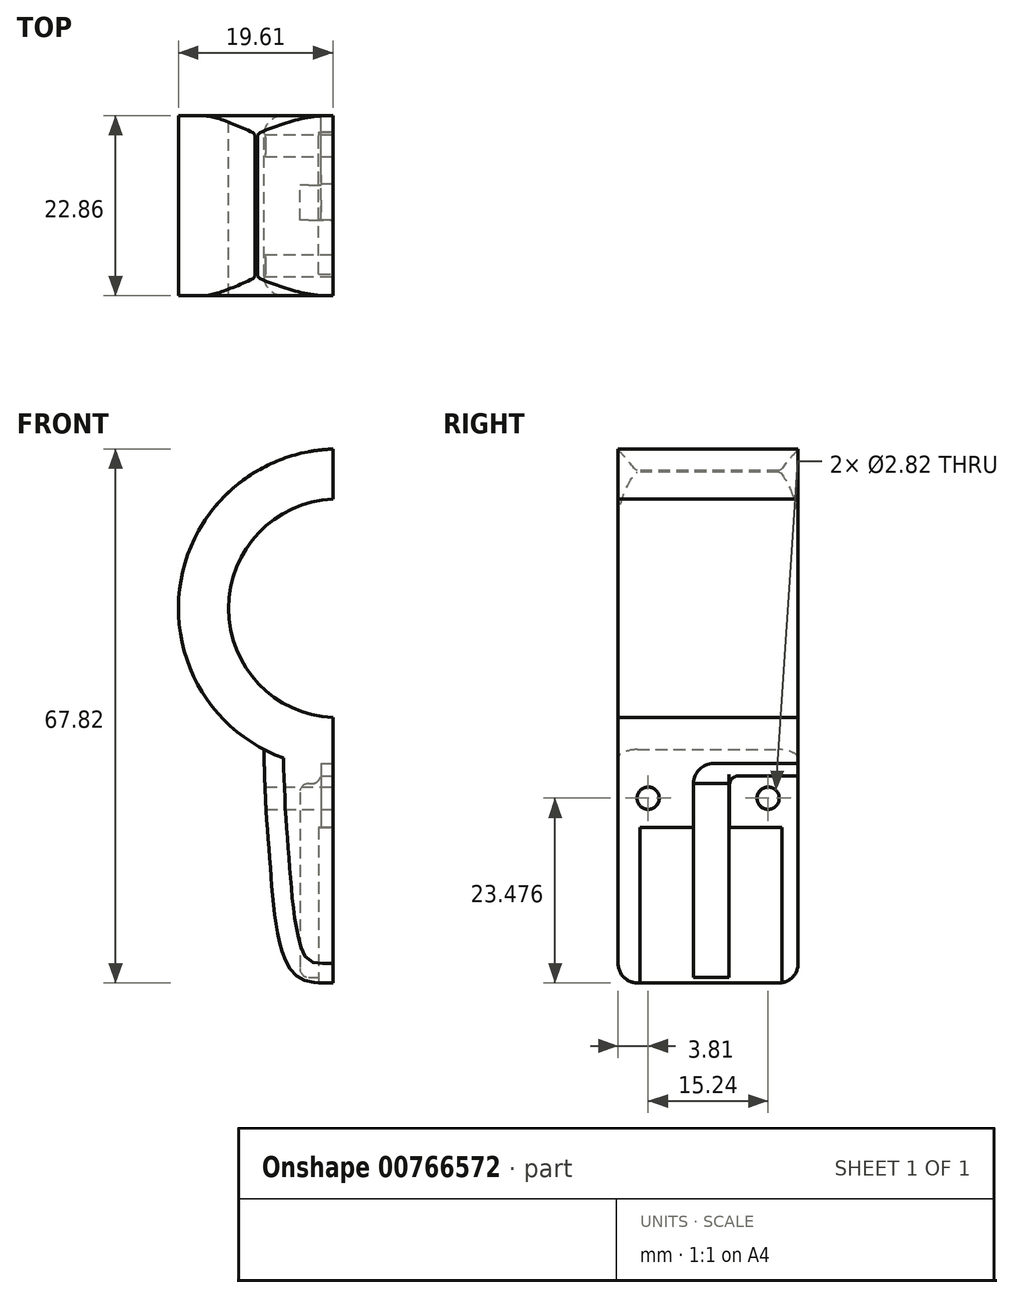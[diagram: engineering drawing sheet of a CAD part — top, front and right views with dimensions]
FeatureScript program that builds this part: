
annotation { "Feature Type Name" : "Feature", "Feature Type Description" : "" }
export const myFeature = defineFeature(function(context is Context, id is Id, definition is map)
    precondition{}
    {
        {
            var Q0;
            Q0=qCreatedBy(makeId("Front.planeOp"),FACE);
            var sketch = newSketch(context, id + "F0", { "sketchPlane" : qUnion([Q0])});
            skCircle(sketch, "E0", {"center": v(0, 0) * mm, "radius": 13.9 * mm});
            skCircle(sketch, "E1.0", {"center": v(0, 0) * mm, "radius": 20.24 * mm});
            skFitSpline(sketch, "E2", {"points": [v(-10.48, 17.32) * mm, v(-6.62, 22.45) * mm, v(-5.79, 30.49) * mm, v(0, 31.88) * mm, v(5.12, 30.56) * mm, v(6.08, 23.46) * mm, v(9.7, 17.76) * mm], "startDerivative": vector(26.15, 14.41) * mm, "endDerivative": vector(40.23, -23.63) * mm});
            skFitSpline(sketch, "E3", {"points": [v(-9.4, -17.93) * mm, v(-8.61, -32.2) * mm, v(-5.82, -46.1) * mm, v(0, -47.57) * mm, v(6.45, -45.96) * mm, v(9.7, -28.64) * mm, v(9.7, -17.76) * mm], "startDerivative": vector(4.47, -161.39) * mm, "endDerivative": vector(-1.33, 64.22) * mm});
            skSolve(sketch);
        }
        {
            var Q0;
            Q0=makeQuery(id+"F0.imprint","IMPRINT",FACE,{"disambiguationData":[TD([[makeQuery(id+"F0.imprint","IMPRINT",EDGE,{"derivedFrom":sQuery(id+"F0.wireOp",EDGE,"E0")}),-1.0]])]});
            var Q1;
            {var subQ0=sQuery(id+"F0.wireOp",EDGE,"E3");Q1=makeQuery(id+"F0.imprint","IMPRINT",FACE,{"disambiguationData":[TD([[makeQuery(id+"F0.imprint","IMPRINT",EDGE,{"derivedFrom":subQ0}),1.0]])]});}
            var Q2;
            {var subQ0=sQuery(id+"F0.wireOp",EDGE,"E2");var subQ1=sQuery(id+"F0.wireOp",EDGE,"E1.0");var subQ2=makeQuery(id+"F0.imprint","INTERSECT",VERTEX,{"disambiguationData":[OD(1.0)],"derivedFrom":[subQ1,subQ0]});Q2=makeQuery(id+"F0.imprint","IMPRINT",FACE,{"disambiguationData":[TD([[makeQuery(id+"F0.imprint","IMPRINT",EDGE,{"disambiguationData":[TD([[subQ2,-1.0]])],"derivedFrom":subQ1}),-1.0]])]});}
            extrude(context, id + "F1", {"entities" : qUnion([Q0, Q1, Q2]), "depth" : 22.86 * mm, "offsetDistance" : 25.4 * mm});
        }
        {
            var Q0;
            Q0=qCreatedBy(makeId("Right.planeOp"),FACE);
            var sketch = newSketch(context, id + "F2", { "sketchPlane" : qUnion([Q0])});
            skCircle(sketch, "E4", {"center": v(-10.97, 26.33) * mm, "radius": 1.9 * mm});
            skCircle(sketch, "E5", {"center": v(-19.05, -24.11) * mm, "radius": 1.41 * mm});
            skCircle(sketch, "E6", {"center": v(-3.81, -24.11) * mm, "radius": 1.41 * mm});
            skSolve(sketch);
        }
        {
            var Q0;
            Q0=qSketchRegion(id+"F2",true);
            extrude(context, id + "F3", {"entities" : qUnion([Q0]), "operationType" : NewBodyOperationType.REMOVE, "endBound" : BoundingType.SYMMETRIC, "oppositeDirection" : true, "depth" : 25.4 * mm, "offsetDistance" : 25.4 * mm});
        }
        {
            var Q0;
            Q0=qCreatedBy(makeId("Front.planeOp"),FACE);
            var sketch = newSketch(context, id + "F4", { "sketchPlane" : qUnion([Q0])});
            skLineSegment(sketch, "E7.bottom", {"start": v(-0.64, 36.94) * mm, "end": v(30.33, 36.94) * mm});
            skLineSegment(sketch, "E7.top", {"start": v(-0.64, -50.47) * mm, "end": v(30.33, -50.47) * mm});
            skLineSegment(sketch, "E7.left", {"start": v(-0.64, 36.94) * mm, "end": v(-0.64, -50.47) * mm});
            skLineSegment(sketch, "E7.right", {"start": v(30.33, 36.94) * mm, "end": v(30.33, -50.47) * mm});
            skSolve(sketch);
        }
        {
            var Q0;
            Q0=makeQuery(id+"F4.imprint","IMPRINT",FACE,{"disambiguationData":[TD([[makeQuery(id+"F4.imprint","IMPRINT",EDGE,{"derivedFrom":sQuery(id+"F4.wireOp",EDGE,"E7.bottom")}),-1.0]])]});
            extrude(context, id + "F5", {"entities" : qUnion([Q0]), "operationType" : NewBodyOperationType.REMOVE, "depth" : 25.4 * mm, "offsetDistance" : 25.4 * mm});
        }
        {
            var Q0;
            Q0=makeQuery(id+"F1.opExtrude","CAP_EDGE",EDGE,{"disambiguationData":[OSD([sQuery(id+"F0.wireOp",EDGE,"E2")])],"isStart":false});
            var Q1;
            {var subQ0=sQuery(id+"F0.wireOp",EDGE,"E1.0");Q1=makeQuery(id+"F1.opExtrude","CAP_EDGE",EDGE,{"disambiguationData":[OSD([subQ0]),TDD([makeQuery(id+"F0.imprint","IMPRINT",EDGE,{"disambiguationData":[TD([[makeQuery(id+"F0.imprint","INTERSECT",VERTEX,{"disambiguationData":[OD(0.0)],"derivedFrom":[subQ0,sQuery(id+"F0.wireOp",EDGE,"E2")]}),-1.0]])],"derivedFrom":subQ0})])],"isStart":false});}
            var Q2;
            Q2=makeQuery(id+"F1.opExtrude","CAP_EDGE",EDGE,{"disambiguationData":[OSD([sQuery(id+"F0.wireOp",EDGE,"E3")])],"isStart":false});
            var Q3;
            Q3=makeQuery(id+"F1.opExtrude","CAP_EDGE",EDGE,{"disambiguationData":[OSD([sQuery(id+"F0.wireOp",EDGE,"E2")])],"isStart":true});
            var Q4;
            {var subQ0=sQuery(id+"F0.wireOp",EDGE,"E1.0");Q4=makeQuery(id+"F1.opExtrude","CAP_EDGE",EDGE,{"disambiguationData":[OSD([subQ0]),TDD([makeQuery(id+"F0.imprint","IMPRINT",EDGE,{"disambiguationData":[TD([[makeQuery(id+"F0.imprint","INTERSECT",VERTEX,{"disambiguationData":[OD(0.0)],"derivedFrom":[subQ0,sQuery(id+"F0.wireOp",EDGE,"E2")]}),-1.0]])],"derivedFrom":subQ0})])],"isStart":true});}
            var Q5;
            Q5=makeQuery(id+"F1.opExtrude","CAP_EDGE",EDGE,{"disambiguationData":[OSD([sQuery(id+"F0.wireOp",EDGE,"E3")])],"isStart":true});
            fillet(context, id + "F6", {"entities" : qUnion([Q0, Q1, Q2, Q3, Q4, Q5]), "radius" : 2.45 * mm, "tangentPropagation" : true, "allowEdgeOverflow" : false});
        }
        {
            var Q0;
            {var subQ1=sQuery(id+"F0.wireOp",EDGE,"E3");Q0=makeQuery(id+"F5.boolean.opBoolean","COPY",FACE,{"disambiguationData":[TD([makeQuery(id+"F1.opExtrude","SWEPT_FACE",FACE,{"disambiguationData":[OSD([subQ1])]})])],"derivedFrom":makeQuery(id+"F5.opExtrude","SWEPT_FACE",FACE,{"disambiguationData":[OSD([sQuery(id+"F4.wireOp",EDGE,"E7.left")])]})});}
            var sketch = newSketch(context, id + "F7", { "sketchPlane" : qUnion([Q0])});
            skLineSegment(sketch, "E8.bottom", {"start": v(-20.1, -27.85) * mm, "end": v(-2.07, -27.85) * mm});
            skLineSegment(sketch, "E8.top", {"start": v(-20.1, -51.03) * mm, "end": v(-2.07, -51.03) * mm});
            skLineSegment(sketch, "E8.left", {"start": v(-20.1, -27.85) * mm, "end": v(-20.1, -51.03) * mm});
            skLineSegment(sketch, "E8.right", {"start": v(-2.07, -27.85) * mm, "end": v(-2.07, -51.03) * mm});
            skSolve(sketch);
        }
        {
            var Q0;
            {var subQ0=sQuery(id+"F7.wireOp",EDGE,"E8.bottom");Q0=makeQuery(id+"F7.imprint","IMPRINT",FACE,{"disambiguationData":[TD([[makeQuery(id+"F7.imprint","IMPRINT",EDGE,{"derivedFrom":subQ0}),-1.0]])]});}
            var Q1;
            {var subQ0=sQuery(id+"F7.wireOp",EDGE,"E8.top");Q1=makeQuery(id+"F7.imprint","IMPRINT",FACE,{"disambiguationData":[TD([[makeQuery(id+"F7.imprint","IMPRINT",EDGE,{"derivedFrom":subQ0}),1.0]])]});}
            extrude(context, id + "F8", {"entities" : qUnion([Q0, Q1]), "operationType" : NewBodyOperationType.REMOVE, "oppositeDirection" : true, "depth" : 1.78 * mm, "offsetDistance" : 25.4 * mm});
        }
        {
            var Q0;
            {var subQ1=sQuery(id+"F0.wireOp",EDGE,"E3");Q0=makeQuery(id+"F5.boolean.opBoolean","COPY",FACE,{"disambiguationData":[TD([makeQuery(id+"F1.opExtrude","SWEPT_FACE",FACE,{"disambiguationData":[OSD([subQ1])]})])],"derivedFrom":makeQuery(id+"F5.opExtrude","SWEPT_FACE",FACE,{"disambiguationData":[OSD([sQuery(id+"F4.wireOp",EDGE,"E7.left")])]})});}
            var sketch = newSketch(context, id + "F9", { "sketchPlane" : qUnion([Q0])});
            skLineSegment(sketch, "E9.bottom", {"start": v(-10.74, -19.72) * mm, "end": v(-8.7, -19.72) * mm});
            skLineSegment(sketch, "E9.top", {"start": v(-13.28, -31.32) * mm, "end": v(-8.7, -31.32) * mm});
            skLineSegment(sketch, "E9.left", {"start": v(-13.28, -22.26) * mm, "end": v(-13.28, -31.32) * mm});
            skLineSegment(sketch, "E9.right", {"start": v(-8.7, -21.27) * mm, "end": v(-8.7, -31.32) * mm});
            skLineSegment(sketch, "E10.bottom", {"start": v(-8.7, -19.72) * mm, "end": v(0.09, -19.72) * mm});
            skLineSegment(sketch, "E10.top", {"start": v(-8.7, -21.27) * mm, "end": v(0.09, -21.27) * mm});
            skLineSegment(sketch, "E10.right", {"start": v(0.09, -19.72) * mm, "end": v(0.09, -21.27) * mm});
            skPoint(sketch, "E11.visualSharp", {"position": v(-13.28, -19.72) * mm});
            skArc(sketch, "E11.filletArc", {"start": v(-10.74, -19.72) * mm, "mid": v(-12.54, -20.47) * mm, "end": v(-13.28, -22.26) * mm});
            skSolve(sketch);
        }
        {
            var Q0;
            {var subQ1=sQuery(id+"F9.wireOp",EDGE,"E9.bottom");Q0=makeQuery(id+"F9.imprint","IMPRINT",FACE,{"disambiguationData":[TD([[makeQuery(id+"F9.imprint","IMPRINT",EDGE,{"derivedFrom":subQ1}),-1.0]])]});}
            var Q1;
            {var subQ0=sQuery(id+"F9.wireOp",EDGE,"E9.top");Q1=makeQuery(id+"F9.imprint","IMPRINT",FACE,{"disambiguationData":[TD([[makeQuery(id+"F9.imprint","IMPRINT",EDGE,{"derivedFrom":subQ0}),1.0]])]});}
            extrude(context, id + "F10", {"entities" : qUnion([Q0, Q1]), "operationType" : NewBodyOperationType.REMOVE, "oppositeDirection" : true, "depth" : 1.52 * mm, "offsetDistance" : 25.4 * mm});
        }
        {
            var Q0;
            {var subQ0=sQuery(id+"F0.wireOp",EDGE,"E3");var subQ3=sQuery(id+"F0.wireOp",EDGE,"E0");var subQ5=makeQuery(id+"F1.opExtrude","SWEPT_FACE",FACE,{"disambiguationData":[OSD([subQ3])]});var subQ7=makeQuery(id+"F1.opExtrude","SWEPT_FACE",FACE,{"disambiguationData":[OSD([subQ0])]});Q0=makeQuery(id+"F10.boolean.opBoolean","SPLIT",FACE,{"disambiguationData":[TD([subQ5])],"derivedFrom":makeQuery(id+"F5.boolean.opBoolean","COPY",FACE,{"disambiguationData":[TD([subQ7])],"derivedFrom":makeQuery(id+"F5.opExtrude","SWEPT_FACE",FACE,{"disambiguationData":[OSD([sQuery(id+"F4.wireOp",EDGE,"E7.left")])]})})});}
            var sketch = newSketch(context, id + "F11", { "sketchPlane" : qUnion([Q0])});
            skLineSegment(sketch, "E12.bottom", {"start": v(-13.28, -22.26) * mm, "end": v(-8.8, -22.26) * mm});
            skLineSegment(sketch, "E12.top", {"start": v(-13.28, -46.86) * mm, "end": v(-8.8, -46.86) * mm});
            skLineSegment(sketch, "E12.left", {"start": v(-13.28, -22.26) * mm, "end": v(-13.28, -46.86) * mm});
            skLineSegment(sketch, "E12.right", {"start": v(-8.8, -22.26) * mm, "end": v(-8.8, -46.86) * mm});
            skSolve(sketch);
        }
        {
            var Q0;
            {var subQ1=sQuery(id+"F11.wireOp",EDGE,"E12.bottom");Q0=makeQuery(id+"F11.imprint","IMPRINT",FACE,{"disambiguationData":[TD([[makeQuery(id+"F11.imprint","IMPRINT",EDGE,{"derivedFrom":subQ1}),-1.0]])]});}
            extrude(context, id + "F12", {"entities" : qUnion([Q0]), "operationType" : NewBodyOperationType.REMOVE, "oppositeDirection" : true, "depth" : 4.2 * mm, "offsetDistance" : 25.4 * mm});
        }
        {
            var Q0;
            Q0=makeQuery(id+"F12.boolean.opBoolean","COPY",EDGE,{"derivedFrom":makeQuery(id+"F12.opExtrude","CAP_EDGE",EDGE,{"disambiguationData":[OSD([sQuery(id+"F11.wireOp",EDGE,"E12.top")])],"isStart":false})});
            var Q1;
            Q1=makeQuery(id+"F12.boolean.opBoolean","COPY",EDGE,{"derivedFrom":makeQuery(id+"F12.opExtrude","CAP_EDGE",EDGE,{"disambiguationData":[OSD([sQuery(id+"F11.wireOp",EDGE,"E12.bottom")])],"isStart":false})});
            var Q2;
            Q2=makeQuery(id+"F12.boolean.opBoolean","INTERSECT",EDGE,{"derivedFrom":[makeQuery(id+"F10.boolean.opBoolean","COPY",FACE,{"derivedFrom":makeQuery(id+"F10.opExtrude","CAP_FACE",FACE,{"disambiguationData":[OSD([sQuery(id+"F4.wireOp",EDGE,"E7.left"),sQuery(id+"F9.wireOp",EDGE,"E9.bottom"),sQuery(id+"F9.wireOp",EDGE,"E9.top"),sQuery(id+"F9.wireOp",EDGE,"E9.left"),sQuery(id+"F9.wireOp",EDGE,"E9.right"),sQuery(id+"F9.wireOp",EDGE,"E10.bottom"),sQuery(id+"F9.wireOp",EDGE,"E10.top"),sQuery(id+"F9.wireOp",EDGE,"E11.filletArc")])],"isStart":false})}),makeQuery(id+"F12.opExtrude","SWEPT_FACE",FACE,{"disambiguationData":[OSD([sQuery(id+"F11.wireOp",EDGE,"E12.bottom")])]})]});
            var Q3;
            Q3=makeQuery(id+"F10.boolean.opBoolean","COPY",EDGE,{"derivedFrom":makeQuery(id+"F10.opExtrude","SWEPT_EDGE",EDGE,{"disambiguationData":[OSD([sQuery(id+"F9.wireOp",EDGE,"E9.right"),sQuery(id+"F9.wireOp",EDGE,"E10.top")])]})});
            fillet(context, id + "F13", {"entities" : qUnion([Q0, Q1, Q2, Q3]), "radius" : 1.13 * mm, "tangentPropagation" : true, "allowEdgeOverflow" : false});
        }
    });
